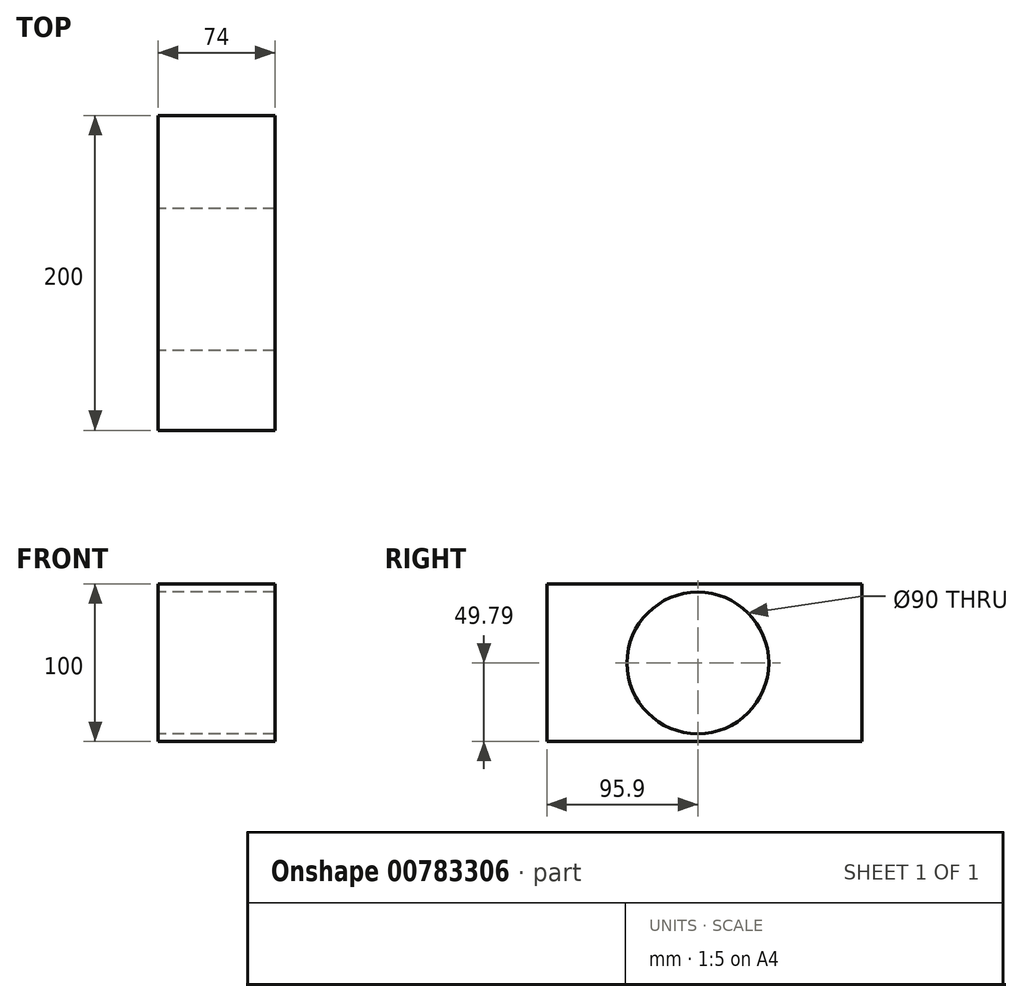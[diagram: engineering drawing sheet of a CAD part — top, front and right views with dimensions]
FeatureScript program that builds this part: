
annotation { "Feature Type Name" : "Feature", "Feature Type Description" : "" }
export const myFeature = defineFeature(function(context is Context, id is Id, definition is map)
    precondition{}
    {
        {
            var Q0;
            Q0=qCreatedBy(makeId("Right.planeOp"),FACE);
            var sketch = newSketch(context, id + "F0", { "sketchPlane" : qUnion([Q0])});
            skCircle(sketch, "E0", {"center": v(0, 0) * mm, "radius": 45 * mm});
            skLineSegment(sketch, "E1.bottom", {"start": v(-95.9, 50.21) * mm, "end": v(104.1, 50.21) * mm});
            skLineSegment(sketch, "E1.top", {"start": v(-95.9, -49.79) * mm, "end": v(104.1, -49.79) * mm});
            skLineSegment(sketch, "E1.left", {"start": v(-95.9, 50.21) * mm, "end": v(-95.9, -49.79) * mm});
            skLineSegment(sketch, "E1.right", {"start": v(104.1, 50.21) * mm, "end": v(104.1, -49.79) * mm});
            skLineSegment(sketch, "E2.bottom", {"start": v(-64.78, 50.21) * mm, "end": v(85.22, 50.21) * mm});
            skLineSegment(sketch, "E2.top", {"start": v(-64.78, -49.79) * mm, "end": v(85.22, -49.79) * mm});
            skLineSegment(sketch, "E2.left", {"start": v(-64.78, 50.21) * mm, "end": v(-64.78, -49.79) * mm});
            skLineSegment(sketch, "E2.right", {"start": v(85.22, 50.21) * mm, "end": v(85.22, -49.79) * mm});
            skSolve(sketch);
        }
        {
            var Q0;
            Q0 = qSketchRegion(id + "F0", true);
            extrude(context, id + "F1", {"entities" : qUnion([Q0]), "depth" : 25 * mm, "offsetDistance" : 25 * mm});
        }
        {
            var Q0;
            Q0=makeQuery(id+"F1.opExtrude","CAP_FACE",FACE,{"disambiguationData":[OSD([sQuery(id+"F0.wireOp",EDGE,"E0"),sQuery(id+"F0.wireOp",EDGE,"E1.bottom"),sQuery(id+"F0.wireOp",EDGE,"E1.top"),sQuery(id+"F0.wireOp",EDGE,"E1.left"),sQuery(id+"F0.wireOp",EDGE,"E1.right"),sQuery(id+"F0.wireOp",EDGE,"E2.bottom"),sQuery(id+"F0.wireOp",EDGE,"E2.top")])],"isStart":true});
            extrude(context, id + "F2", {"entities" : qUnion([Q0]), "operationType" : NewBodyOperationType.ADD, "depth" : 49 * mm, "offsetDistance" : 25 * mm});
        }
    });
